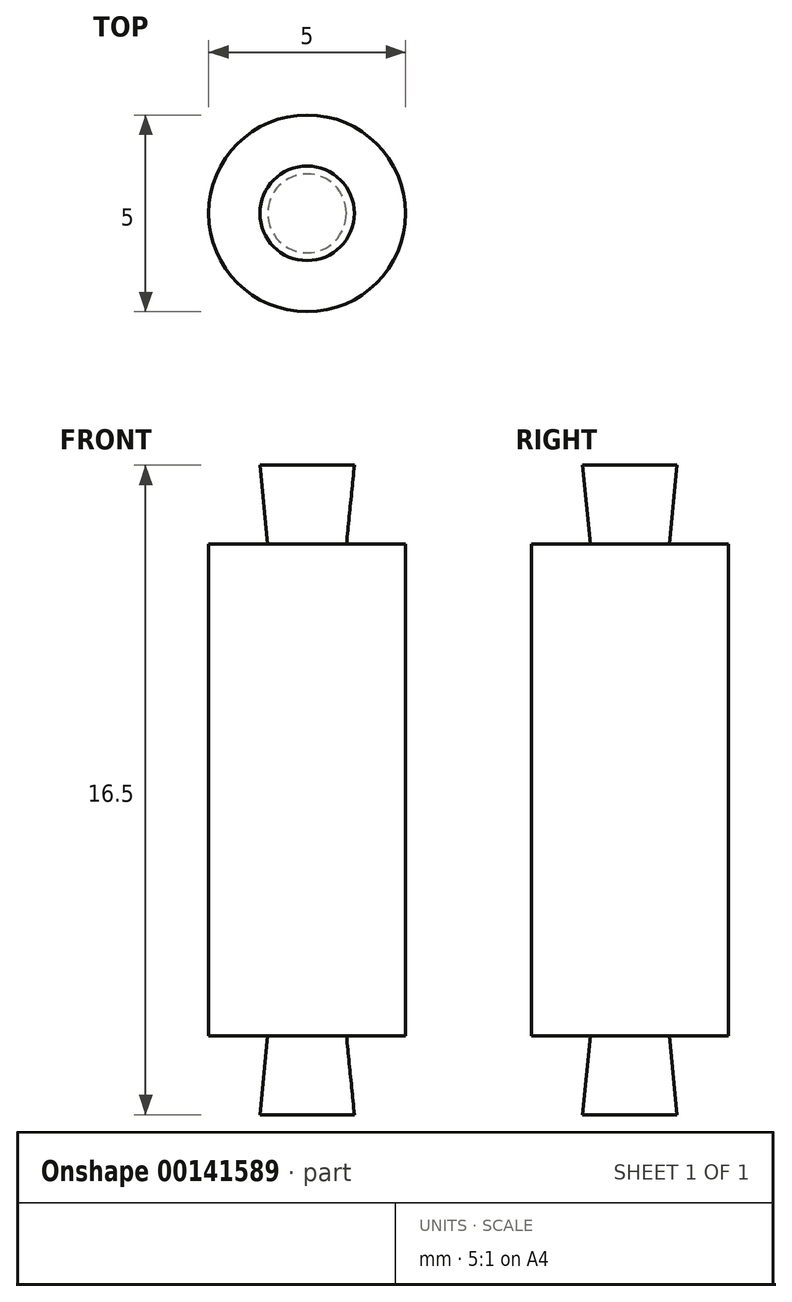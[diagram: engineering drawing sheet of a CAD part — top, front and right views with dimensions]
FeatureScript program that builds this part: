
annotation { "Feature Type Name" : "Feature", "Feature Type Description" : "" }
export const myFeature = defineFeature(function(context is Context, id is Id, definition is map)
    precondition{}
    {
        {
            var Q0;
            Q0=qCreatedBy(makeId("Front.planeOp"),FACE);
            var sketch = newSketch(context, id + "F0", { "sketchPlane" : qUnion([Q0])});
            skLineSegment(sketch, "E0", {"start": v(0, 0) * mm, "end": v(-1.2, 0) * mm});
            skLineSegment(sketch, "E1", {"start": v(-1.2, 0) * mm, "end": v(-1, 2) * mm});
            skLineSegment(sketch, "E2", {"start": v(-1, 14.5) * mm, "end": v(-1.2, 16.5) * mm});
            skLineSegment(sketch, "E3", {"start": v(-1.2, 16.5) * mm, "end": v(0, 16.5) * mm});
            skLineSegment(sketch, "E4", {"start": v(-1, 14.5) * mm, "end": v(-2.5, 14.5) * mm});
            skLineSegment(sketch, "E5", {"start": v(-2.5, 14.5) * mm, "end": v(-2.5, 2) * mm});
            skLineSegment(sketch, "E6", {"start": v(-2.5, 2) * mm, "end": v(-1, 2) * mm});
            skLineSegment(sketch, "E7", {"start": v(0, 16.5) * mm, "end": v(0, 0) * mm});
            skSolve(sketch);
        }
        {
            var Q0;
            Q0=makeQuery(id+"F0.imprint","IMPRINT",FACE,{"disambiguationData":[TD([[makeQuery(id+"F0.imprint","IMPRINT",EDGE,{"derivedFrom":sQuery(id+"F0.wireOp",EDGE,"E0")}),-1.0]])]});
            var Q1;
            Q1=sQuery(id+"F0.wireOp",EDGE,"E7");
            revolve(context, id + "F1", {"entities" : qUnion([Q0]), "axis" : qUnion([Q1]), "revolveType" : RevolveType.FULL});
        }
    });
